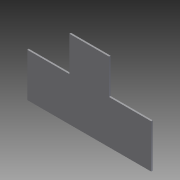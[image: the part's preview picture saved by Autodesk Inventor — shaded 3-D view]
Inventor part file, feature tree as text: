
AUTODESK INVENTOR PART (.ipt)
format: ipt  version: 2011 (Build 150239000, 239)  size: 384,512 bytes
history: native  units: in
note: dims shown in document units (in); Inventor stores cm internally (conversion verified against a paired STEP export)
features: extrude x13, sketch x13
ambient origin geometry x8: Origin, YZ Plane, XZ Plane, XY Plane, X Axis, Y Axis, Z Axis, Center Point
bodies: Solid1 (feature_tree)
feature tree (26):
  extrude  "Extrusion1"  Depth=12.85in
  extrude  "Extrusion2"  Depth=0.75in
  extrude  "Extrusion3"  Depth=2.0in
  extrude  "Extrusion4"  Depth=2.0in
  extrude  "Extrusion5"  Depth=2.0in
  extrude  "Extrusion6"  Depth=2.0in
  extrude  "Extrusion7"  Depth=2.0in
  extrude  "Extrusion8"  Depth=0.75in
  extrude  "Extrusion9"  Depth=0.25in TaperAngle=0.0deg
  extrude  "Extrusion10"  Depth=2.0in
  extrude  "Extrusion11"  Depth=7.175in
  extrude  "Extrusion12"  Depth=2.0in
  extrude  "Extrusion13"  Depth=2.0in
  sketch  "Sketch1"  dims[d0=19.5in d1=12.85in]
  sketch  "Sketch2"  dims[d2=0.25in d3=0.0in d4=0.75in]
  sketch  "Sketch3"  dims[d5=0.25in d6=2.0in]
  sketch  "Sketch4"  dims[d7=2.0in d8=2.0in]
  sketch  "Sketch5"  dims[d9=2.0in d10=2.0in]
  sketch  "Sketch6"  dims[d11=2.0in d12=2.0in]
  sketch  "Sketch7"  dims[d13=2.0in d14=2.0in]
  sketch  "Sketch8"  dims[d15=0.25in d16=0.0in d17=0.75in]
  sketch  "Sketch9"  dims[d18=0.25in d19=0.25in d20=0.0in]
  sketch  "Sketch10"  dims[d21=2.0in d22=2.0in]
  sketch  "Sketch11"  dims[d23=0.25in d24=0.0in d25=7.175in]
  sketch  "Sketch12"  dims[d26=0.25in d27=2.0in]
  sketch  "Sketch13"  dims[d28=2.0in d29=2.0in d30=2.0in d31=2.0in d32=0.25in d33=0.25in d34=0.0in d35=0.25in d36=0.0in d37=3.0in d38=3.0in d39=3.0in d40=3.0in d41=2.0in d42=2.0in d43=1.0in d44=0.0in d45=0.25in d46=0.0in d47=1.0in d48=0.0in d49=1.0in d50=0.0in d51=0.25in d52=0.0in d53=5.5in d54=6.63in d55=6.63in d56=5.5in d57=1.0in d58=0.0in d59=1.0in d60=0.0in]
